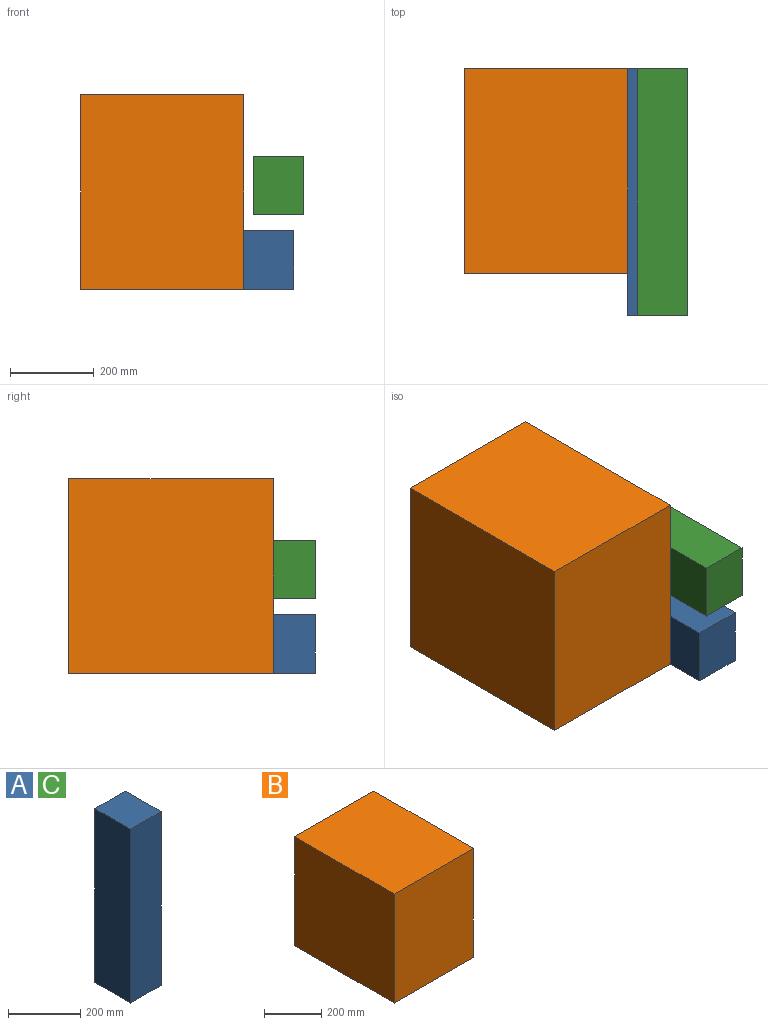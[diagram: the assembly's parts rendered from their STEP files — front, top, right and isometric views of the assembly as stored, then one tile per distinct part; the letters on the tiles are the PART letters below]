
ASSEMBLY  parts=3 mates=1
PART A: 6 faces, bbox 120x140x590 mm
  f0: plane 590x140mm, normal (-1,0,0), area 82600mm2, adj f1,f3,f4,f5
  f1: plane 140x120mm, normal (0,0,-1), area 16800mm2, adj f0,f2,f4,f5
  f2: plane 590x140mm, normal (1,0,0), area 82600mm2, adj f1,f3,f4,f5
  f3: plane 140x120mm, normal (0,0,1), area 16800mm2, adj f0,f2,f4,f5
  f4: plane 590x120mm, normal (0,-1,0), area 70800mm2, adj f0,f1,f2,f3
  f5: plane 590x120mm, normal (0,1,0), area 70800mm2, adj f0,f1,f2,f3
PART B: 6 faces, bbox 390x490x465 mm
  f0: plane 490x390mm, normal (0,0,1), area 191100mm2, adj f1,f3,f4,f5
  f1: plane 490x465mm, normal (-1,0,0), area 227850mm2, adj f0,f2,f4,f5
  f2: plane 490x390mm, normal (0,0,-1), area 191100mm2, adj f1,f3,f4,f5
  f3: plane 490x465mm, normal (1,0,0), area 227850mm2, adj f0,f2,f4,f5
  f4: plane 465x390mm, normal (0,-1,0), area 181350mm2, adj f0,f1,f2,f3
  f5: plane 465x390mm, normal (0,1,0), area 181350mm2, adj f0,f1,f2,f3
PART C: same geometry as A
PLACE A rot(axis=(1,0,0),90deg) t=(-76.81,-220.71,-92.5)mm
PLACE B at identity
PLACE C rot(axis=(0,0.71,-0.71),180deg) t=(610.02,-220.8,-54)mm
MATE fastened A.f0 <-> B.f3  axis (-1,0,0) through (195,0,-232.5)mm
